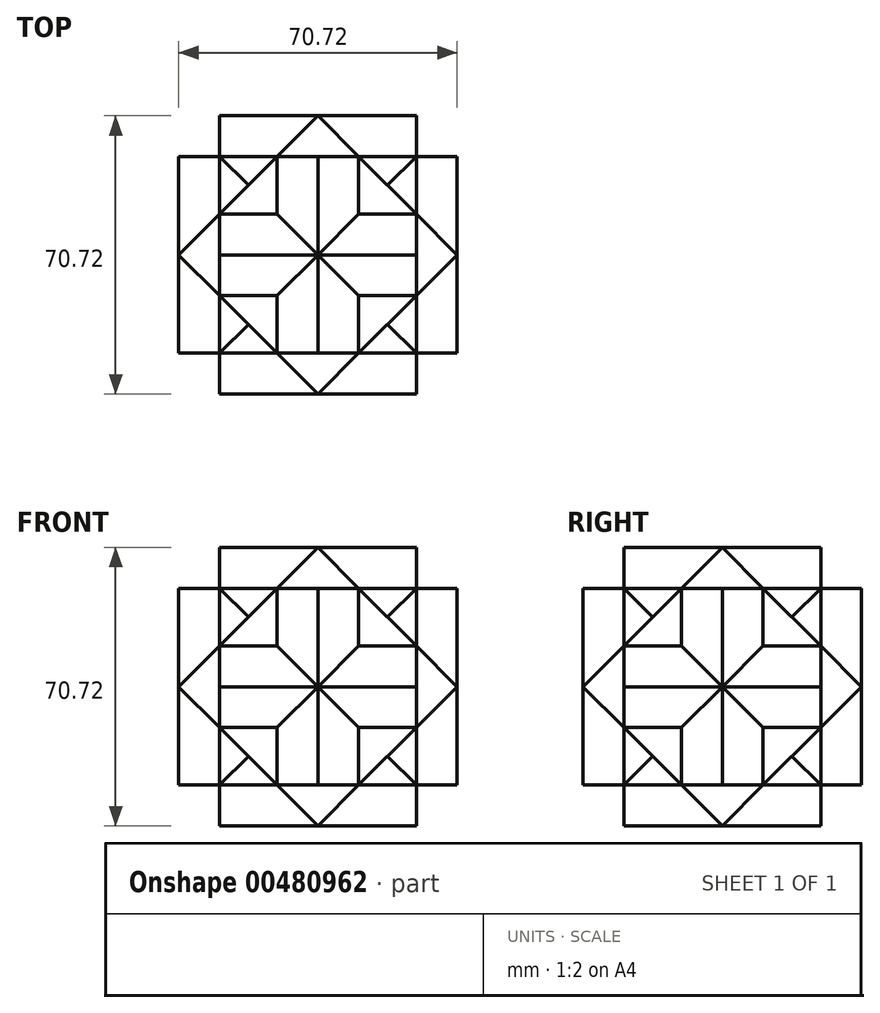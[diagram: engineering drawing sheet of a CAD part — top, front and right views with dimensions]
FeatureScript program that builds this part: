
annotation { "Feature Type Name" : "Feature", "Feature Type Description" : "" }
export const myFeature = defineFeature(function(context is Context, id is Id, definition is map)
    precondition{}
    {
        {
            var Q0;
            Q0=qCreatedBy(makeId("Front.planeOp"),FACE);
            var sketch = newSketch(context, id + "F0", { "sketchPlane" : qUnion([Q0])});
            skLineSegment(sketch, "E0", {"start": v(0, 35.36) * mm, "end": v(35.36, 0) * mm});
            skLineSegment(sketch, "E1", {"start": v(35.36, 0) * mm, "end": v(0, -35.36) * mm});
            skLineSegment(sketch, "E2", {"start": v(0, -35.36) * mm, "end": v(-35.36, 0) * mm});
            skLineSegment(sketch, "E3", {"start": v(-35.36, 0) * mm, "end": v(0, 35.36) * mm});
            skSolve(sketch);
        }
        {
            var Q0;
            Q0=makeQuery(id+"F0.imprint","IMPRINT",FACE,{"disambiguationData":[TD([[makeQuery(id+"F0.imprint","IMPRINT",EDGE,{"derivedFrom":sQuery(id+"F0.wireOp",EDGE,"E0")}),-1.0]])]});
            extrude(context, id + "F1", {"entities" : qUnion([Q0]), "endBound" : BoundingType.SYMMETRIC, "depth" : 50 * mm});
        }
        {
            var Q0;
            Q0=qCreatedBy(makeId("Right.planeOp"),FACE);
            var sketch = newSketch(context, id + "F2", { "sketchPlane" : qUnion([Q0])});
            skLineSegment(sketch, "E4", {"start": v(0, 35.36) * mm, "end": v(35.36, 0) * mm});
            skLineSegment(sketch, "E5", {"start": v(35.36, 0) * mm, "end": v(0, -35.36) * mm});
            skLineSegment(sketch, "E6", {"start": v(0, -35.36) * mm, "end": v(-35.36, 0) * mm});
            skLineSegment(sketch, "E7", {"start": v(-35.36, 0) * mm, "end": v(0, 35.36) * mm});
            skSolve(sketch);
        }
        {
            var Q0;
            Q0=makeQuery(id+"F2.imprint","IMPRINT",FACE,{"disambiguationData":[TD([[makeQuery(id+"F2.imprint","IMPRINT",EDGE,{"derivedFrom":sQuery(id+"F2.wireOp",EDGE,"E4")}),-1.0]])]});
            extrude(context, id + "F3", {"entities" : qUnion([Q0]), "operationType" : NewBodyOperationType.ADD, "endBound" : BoundingType.SYMMETRIC, "depth" : 50 * mm});
        }
        {
            var Q0;
            Q0=qCreatedBy(makeId("Top.planeOp"),FACE);
            var sketch = newSketch(context, id + "F4", { "sketchPlane" : qUnion([Q0])});
            skLineSegment(sketch, "E8", {"start": v(0, -35.36) * mm, "end": v(-35.36, 0) * mm});
            skLineSegment(sketch, "E9", {"start": v(-35.36, 0) * mm, "end": v(0, 35.36) * mm});
            skLineSegment(sketch, "E10", {"start": v(0, 35.36) * mm, "end": v(35.36, 0) * mm});
            skLineSegment(sketch, "E11", {"start": v(35.36, 0) * mm, "end": v(0, -35.36) * mm});
            skSolve(sketch);
        }
        {
            var Q0;
            Q0 = qSketchRegion(id + "F4", true);
            extrude(context, id + "F5", {"entities" : qUnion([Q0]), "operationType" : NewBodyOperationType.ADD, "endBound" : BoundingType.SYMMETRIC, "depth" : 50 * mm});
        }
    });
